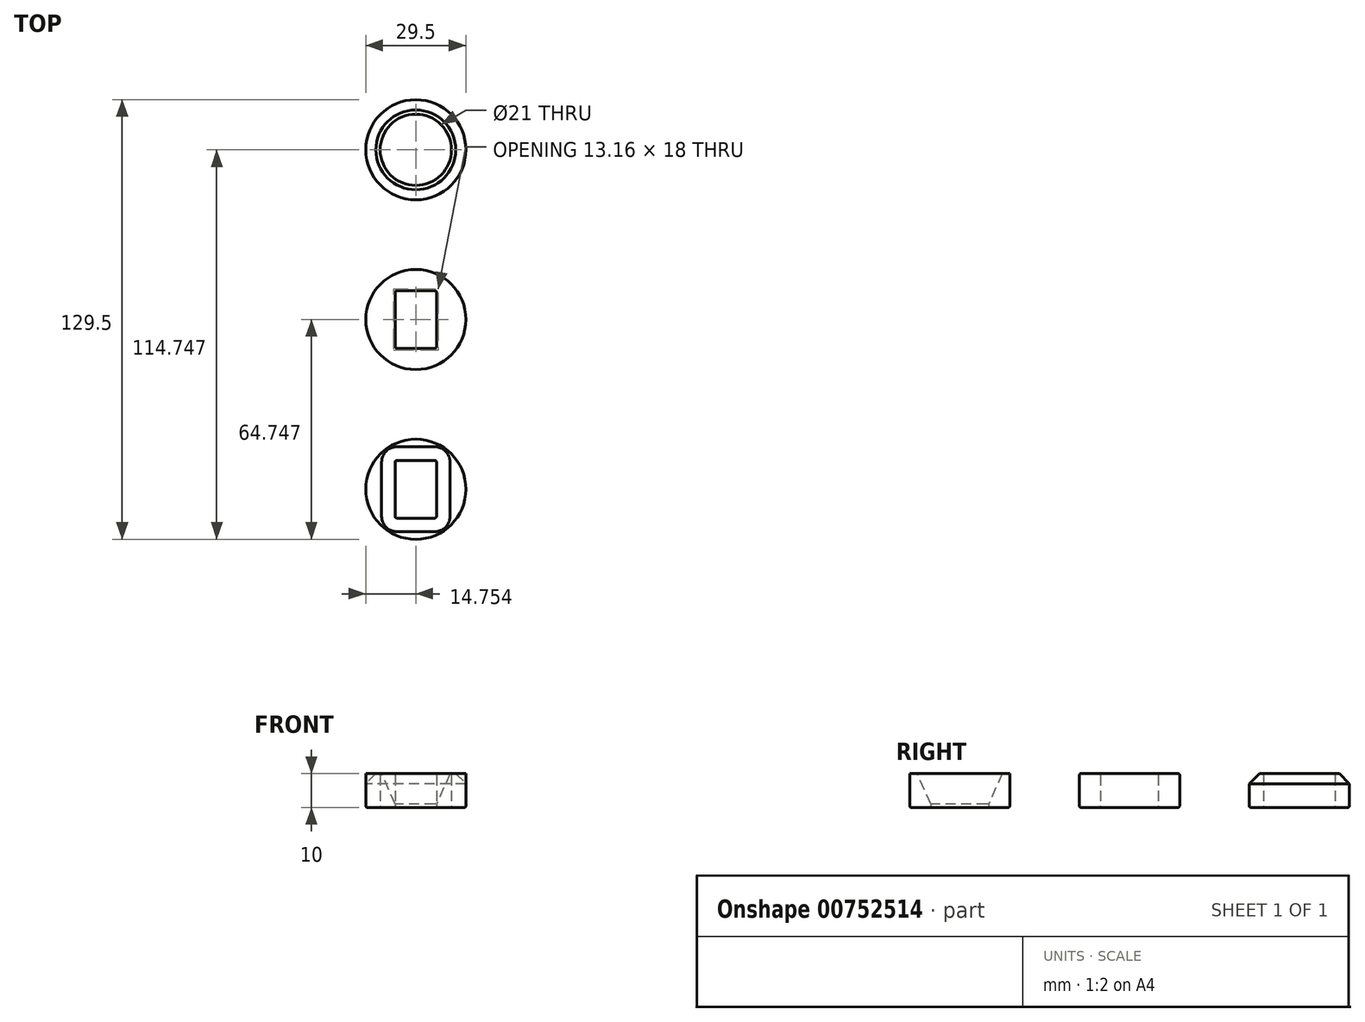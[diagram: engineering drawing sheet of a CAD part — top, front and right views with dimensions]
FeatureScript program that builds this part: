
annotation { "Feature Type Name" : "Feature", "Feature Type Description" : "" }
export const myFeature = defineFeature(function(context is Context, id is Id, definition is map)
    precondition{}
    {
        {
            var Q0;
            Q0=qCreatedBy(makeId("Top.planeOp"),FACE);
            var sketch = newSketch(context, id + "F0", { "sketchPlane" : qUnion([Q0])});
            skCircle(sketch, "E0", {"center": v(-115.66, 28.39) * mm, "radius": 10.5 * mm});
            skCircle(sketch, "E1", {"center": v(-115.66, 28.39) * mm, "radius": 14.75 * mm});
            skCircle(sketch, "E2", {"center": v(-115.66, -21.61) * mm, "radius": 14.75 * mm});
            skLineSegment(sketch, "E3.bottom", {"start": v(-121.74, -13.11) * mm, "end": v(-109.57, -13.11) * mm});
            skLineSegment(sketch, "E3.top", {"start": v(-121.74, -30.11) * mm, "end": v(-109.57, -30.11) * mm});
            skLineSegment(sketch, "E3.left", {"start": v(-121.74, -13.11) * mm, "end": v(-121.74, -30.11) * mm});
            skLineSegment(sketch, "E3.right", {"start": v(-109.57, -13.11) * mm, "end": v(-109.57, -30.11) * mm});
            skLineSegment(sketch, "E4", {"start": v(-121.74, -30.11) * mm, "end": v(-109.57, -13.11) * mm, "construction": true});
            skCircle(sketch, "E5", {"center": v(-115.66, -71.61) * mm, "radius": 14.75 * mm});
            skLineSegment(sketch, "E6.bottom", {"start": v(-121.74, -63.11) * mm, "end": v(-109.57, -63.11) * mm});
            skLineSegment(sketch, "E6.top", {"start": v(-121.74, -80.11) * mm, "end": v(-109.57, -80.11) * mm});
            skLineSegment(sketch, "E6.left", {"start": v(-121.74, -63.11) * mm, "end": v(-121.74, -80.11) * mm});
            skLineSegment(sketch, "E6.right", {"start": v(-109.57, -63.11) * mm, "end": v(-109.57, -80.11) * mm});
            skLineSegment(sketch, "E7", {"start": v(-121.74, -80.11) * mm, "end": v(-109.57, -63.11) * mm, "construction": true});
            skSolve(sketch);
        }
        {
            var Q0;
            Q0=makeQuery(id+"F0.imprint","IMPRINT",FACE,{"disambiguationData":[TD([[makeQuery(id+"F0.imprint","IMPRINT",EDGE,{"derivedFrom":sQuery(id+"F0.wireOp",EDGE,"E0")}),-1.0]])]});
            var Q1;
            Q1=makeQuery(id+"F0.imprint","IMPRINT",FACE,{"disambiguationData":[TD([[makeQuery(id+"F0.imprint","IMPRINT",EDGE,{"derivedFrom":sQuery(id+"F0.wireOp",EDGE,"E2")}),1.0]])]});
            extrude(context, id + "F1", {"entities" : qUnion([Q0, Q1]), "depth" : 10 * mm, "offsetDistance" : 25 * mm});
        }
        {
            var Q0;
            Q0=makeQuery(id+"F0.imprint","IMPRINT",FACE,{"disambiguationData":[TD([[makeQuery(id+"F0.imprint","IMPRINT",EDGE,{"derivedFrom":sQuery(id+"F0.wireOp",EDGE,"E5")}),1.0]])]});
            extrude(context, id + "F2", {"entities" : qUnion([Q0]), "depth" : 10 * mm, "offsetDistance" : 25 * mm});
        }
        {
            var Q0;
            Q0=makeQuery(id+"F1.opExtrude","CAP_EDGE",EDGE,{"disambiguationData":[OSD([sQuery(id+"F0.wireOp",EDGE,"E1")])],"isStart":false});
            chamfer(context, id + "F3", {"entities" : qUnion([Q0]), "width" : 3 * mm, "tangentPropagation" : true});
        }
        {
            var Q0;
            Q0=makeQuery(id+"F1.opExtrude","CAP_FACE",FACE,{"disambiguationData":[OSD([sQuery(id+"F0.wireOp",EDGE,"E2"),sQuery(id+"F0.wireOp",EDGE,"E3.bottom"),sQuery(id+"F0.wireOp",EDGE,"E3.top"),sQuery(id+"F0.wireOp",EDGE,"E3.left"),sQuery(id+"F0.wireOp",EDGE,"E3.right")])],"isStart":true});
            var Q1;
            Q1=makeQuery(id+"F1.opExtrude","CAP_FACE",FACE,{"disambiguationData":[OSD([sQuery(id+"F0.wireOp",EDGE,"E0"),sQuery(id+"F0.wireOp",EDGE,"E1")])],"isStart":true});
            var Q2;
            Q2=makeQuery(id+"F1.opExtrude","CAP_FACE",FACE,{"disambiguationData":[OSD([sQuery(id+"F0.wireOp",EDGE,"E2"),sQuery(id+"F0.wireOp",EDGE,"E3.bottom"),sQuery(id+"F0.wireOp",EDGE,"E3.top"),sQuery(id+"F0.wireOp",EDGE,"E3.left"),sQuery(id+"F0.wireOp",EDGE,"E3.right")])],"isStart":false});
            var Q3;
            Q3=makeQuery(id+"F1.opExtrude","SWEPT_FACE",FACE,{"disambiguationData":[OSD([sQuery(id+"F0.wireOp",EDGE,"E3.bottom")])]});
            var Q4;
            Q4=makeQuery(id+"F1.opExtrude","SWEPT_FACE",FACE,{"disambiguationData":[OSD([sQuery(id+"F0.wireOp",EDGE,"E3.top")])]});
            var Q5;
            Q5=makeQuery(id+"F1.opExtrude","SWEPT_FACE",FACE,{"disambiguationData":[OSD([sQuery(id+"F0.wireOp",EDGE,"E3.right")])]});
            var Q6;
            Q6=makeQuery(id+"F1.opExtrude","SWEPT_FACE",FACE,{"disambiguationData":[OSD([sQuery(id+"F0.wireOp",EDGE,"E3.left")])]});
            var Q7;
            Q7=makeQuery(id+"F1.opExtrude","SWEPT_FACE",FACE,{"disambiguationData":[OSD([sQuery(id+"F0.wireOp",EDGE,"E0")])]});
            var Q8;
            Q8=makeQuery(id+"F2.opExtrude","CAP_FACE",FACE,{"disambiguationData":[OSD([sQuery(id+"F0.wireOp",EDGE,"E5"),sQuery(id+"F0.wireOp",EDGE,"E6.bottom"),sQuery(id+"F0.wireOp",EDGE,"E6.top"),sQuery(id+"F0.wireOp",EDGE,"E6.left"),sQuery(id+"F0.wireOp",EDGE,"E6.right")])],"isStart":true});
            var Q9;
            Q9=makeQuery(id+"F2.opExtrude","SWEPT_EDGE",EDGE,{"disambiguationData":[OSD([sQuery(id+"F0.wireOp",EDGE,"E6.bottom"),sQuery(id+"F0.wireOp",EDGE,"E6.right")])]});
            var Q10;
            Q10=makeQuery(id+"F2.opExtrude","SWEPT_EDGE",EDGE,{"disambiguationData":[OSD([sQuery(id+"F0.wireOp",EDGE,"E6.bottom"),sQuery(id+"F0.wireOp",EDGE,"E6.left")])]});
            var Q11;
            Q11=makeQuery(id+"F2.opExtrude","SWEPT_EDGE",EDGE,{"disambiguationData":[OSD([sQuery(id+"F0.wireOp",EDGE,"E6.top"),sQuery(id+"F0.wireOp",EDGE,"E6.left")])]});
            var Q12;
            Q12=makeQuery(id+"F2.opExtrude","SWEPT_EDGE",EDGE,{"disambiguationData":[OSD([sQuery(id+"F0.wireOp",EDGE,"E6.top"),sQuery(id+"F0.wireOp",EDGE,"E6.right")])]});
            fillet(context, id + "F4", {"entities" : qUnion([Q0, Q1, Q2, Q3, Q4, Q5, Q6, Q7, Q8, Q9, Q10, Q11, Q12]), "radius" : .5 * mm, "tangentPropagation" : true, "allowEdgeOverflow" : false});
        }
        {
            var Q0;
            Q0=makeQuery(id+"F2.opExtrude","CAP_EDGE",EDGE,{"disambiguationData":[OSD([sQuery(id+"F0.wireOp",EDGE,"E6.bottom")])],"isStart":false});
            var Q1;
            Q1=makeQuery(id+"F2.opExtrude","CAP_EDGE",EDGE,{"disambiguationData":[OSD([sQuery(id+"F0.wireOp",EDGE,"E6.right")])],"isStart":false});
            var Q2;
            Q2=makeQuery(id+"F2.opExtrude","CAP_EDGE",EDGE,{"disambiguationData":[OSD([sQuery(id+"F0.wireOp",EDGE,"E6.top")])],"isStart":false});
            var Q3;
            Q3=makeQuery(id+"F2.opExtrude","CAP_EDGE",EDGE,{"disambiguationData":[OSD([sQuery(id+"F0.wireOp",EDGE,"E6.left")])],"isStart":false});
            chamfer(context, id + "F5", {"entities" : qUnion([Q0, Q1, Q2, Q3]), "chamferType" : ChamferType.TWO_OFFSETS, "width1" : 4 * mm, "oppositeDirection" : false, "width2" : 9 * mm, "tangentPropagation" : true});
        }
    });
